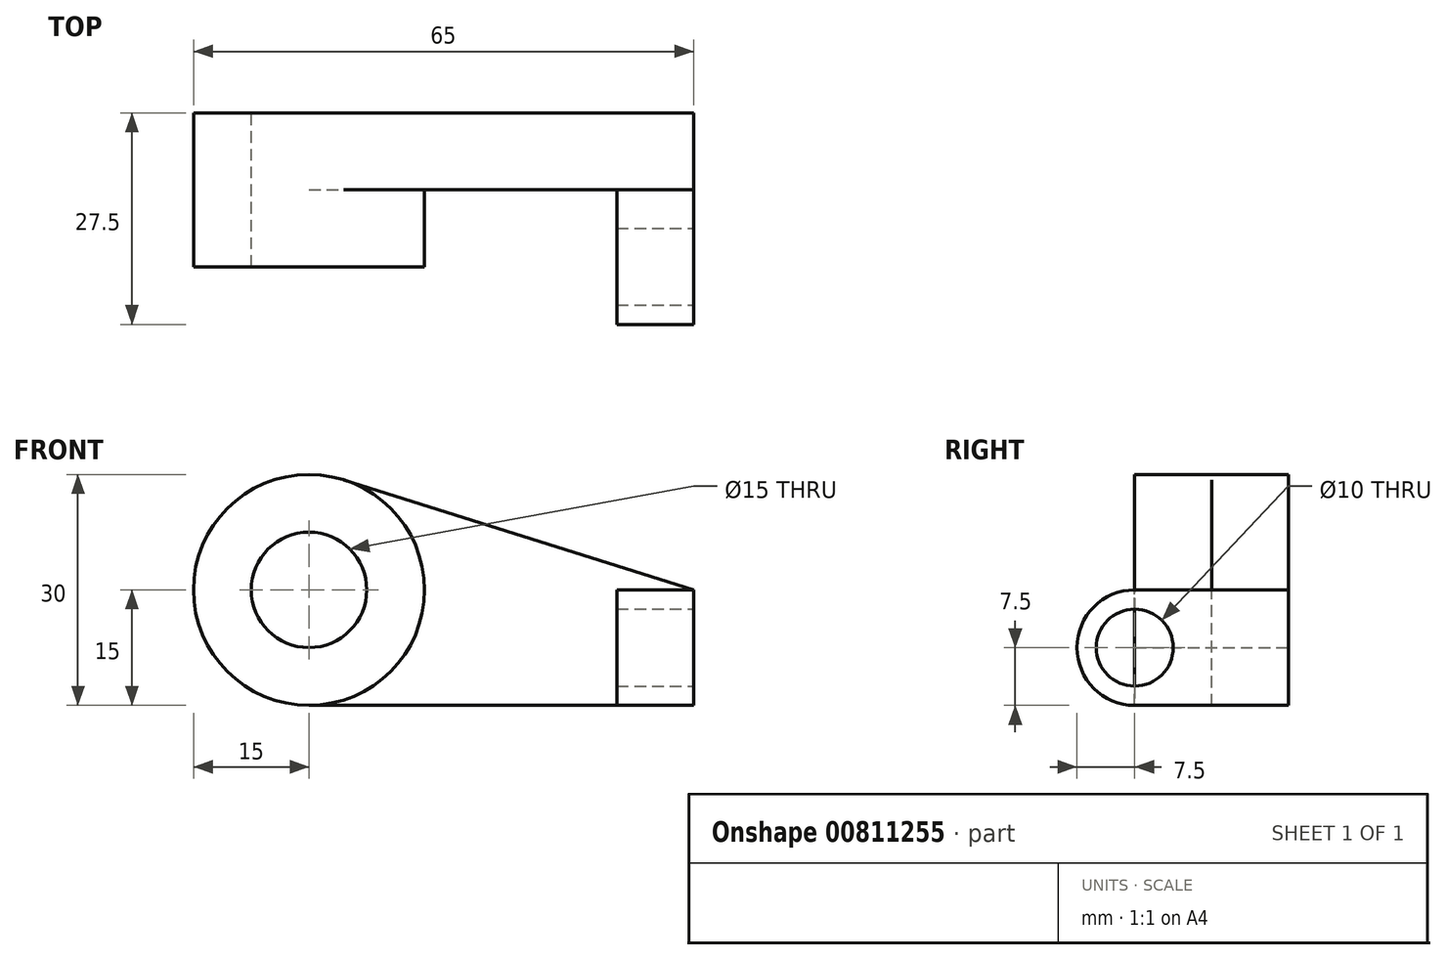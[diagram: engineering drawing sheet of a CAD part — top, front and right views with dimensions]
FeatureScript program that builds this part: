
annotation { "Feature Type Name" : "Feature", "Feature Type Description" : "" }
export const myFeature = defineFeature(function(context is Context, id is Id, definition is map)
    precondition{}
    {
        {
            var Q0;
            Q0=qCreatedBy(makeId("Front.planeOp"),FACE);
            var sketch = newSketch(context, id + "F0", { "sketchPlane" : qUnion([Q0])});
            skCircle(sketch, "E0", {"center": v(0, 0) * mm, "radius": 7.5 * mm});
            skCircle(sketch, "E1", {"center": v(0, 0) * mm, "radius": 15 * mm});
            skLineSegment(sketch, "E2", {"start": v(0, -15) * mm, "end": v(50, -15) * mm});
            skLineSegment(sketch, "E3", {"start": v(50, -15) * mm, "end": v(50, 0) * mm});
            skLineSegment(sketch, "E4", {"start": v(50, 0) * mm, "end": v(4.5, 14.3) * mm});
            skSolve(sketch);
        }
        {
            var Q0;
            Q0 = qSketchRegion(id + "F0", true);
            extrude(context, id + "F1", {"entities" : qUnion([Q0]), "depth" : 10 * mm, "offsetDistance" : 25 * mm});
        }
        {
            var Q0;
            Q0=makeQuery(id+"F0.imprint","IMPRINT",FACE,{"disambiguationData":[TD([[makeQuery(id+"F0.imprint","IMPRINT",EDGE,{"derivedFrom":sQuery(id+"F0.wireOp",EDGE,"E0")}),-1.0]])]});
            extrude(context, id + "F2", {"entities" : qUnion([Q0]), "operationType" : NewBodyOperationType.ADD, "depth" : 20 * mm, "offsetDistance" : 25 * mm});
        }
        {
            var Q0;
            Q0=makeQuery(id+"F1.opExtrude","SWEPT_FACE",FACE,{"disambiguationData":[OSD([sQuery(id+"F0.wireOp",EDGE,"E3")])]});
            var sketch = newSketch(context, id + "F3", { "sketchPlane" : qUnion([Q0])});
            skLineSegment(sketch, "E5.bottom", {"start": v(0, -15) * mm, "end": v(-20, -15) * mm});
            skLineSegment(sketch, "E5.top", {"start": v(0, 0) * mm, "end": v(-20, 0) * mm});
            skLineSegment(sketch, "E5.left", {"start": v(0, -15) * mm, "end": v(0, 0) * mm});
            skLineSegment(sketch, "E5.right", {"start": v(-20, -15) * mm, "end": v(-20, 0) * mm, "construction": true});
            skArc(sketch, "E6", {"start": v(-20, 0) * mm, "mid": v(-27.5, -7.5) * mm, "end": v(-20, -15) * mm});
            skCircle(sketch, "E7", {"center": v(-20, -7.5) * mm, "radius": 5 * mm});
            skSolve(sketch);
        }
        {
            var Q0;
            Q0 = qSketchRegion(id + "F3", true);
            extrude(context, id + "F4", {"entities" : qUnion([Q0]), "operationType" : NewBodyOperationType.ADD, "oppositeDirection" : true, "depth" : 10 * mm, "offsetDistance" : 25 * mm});
        }
    });
